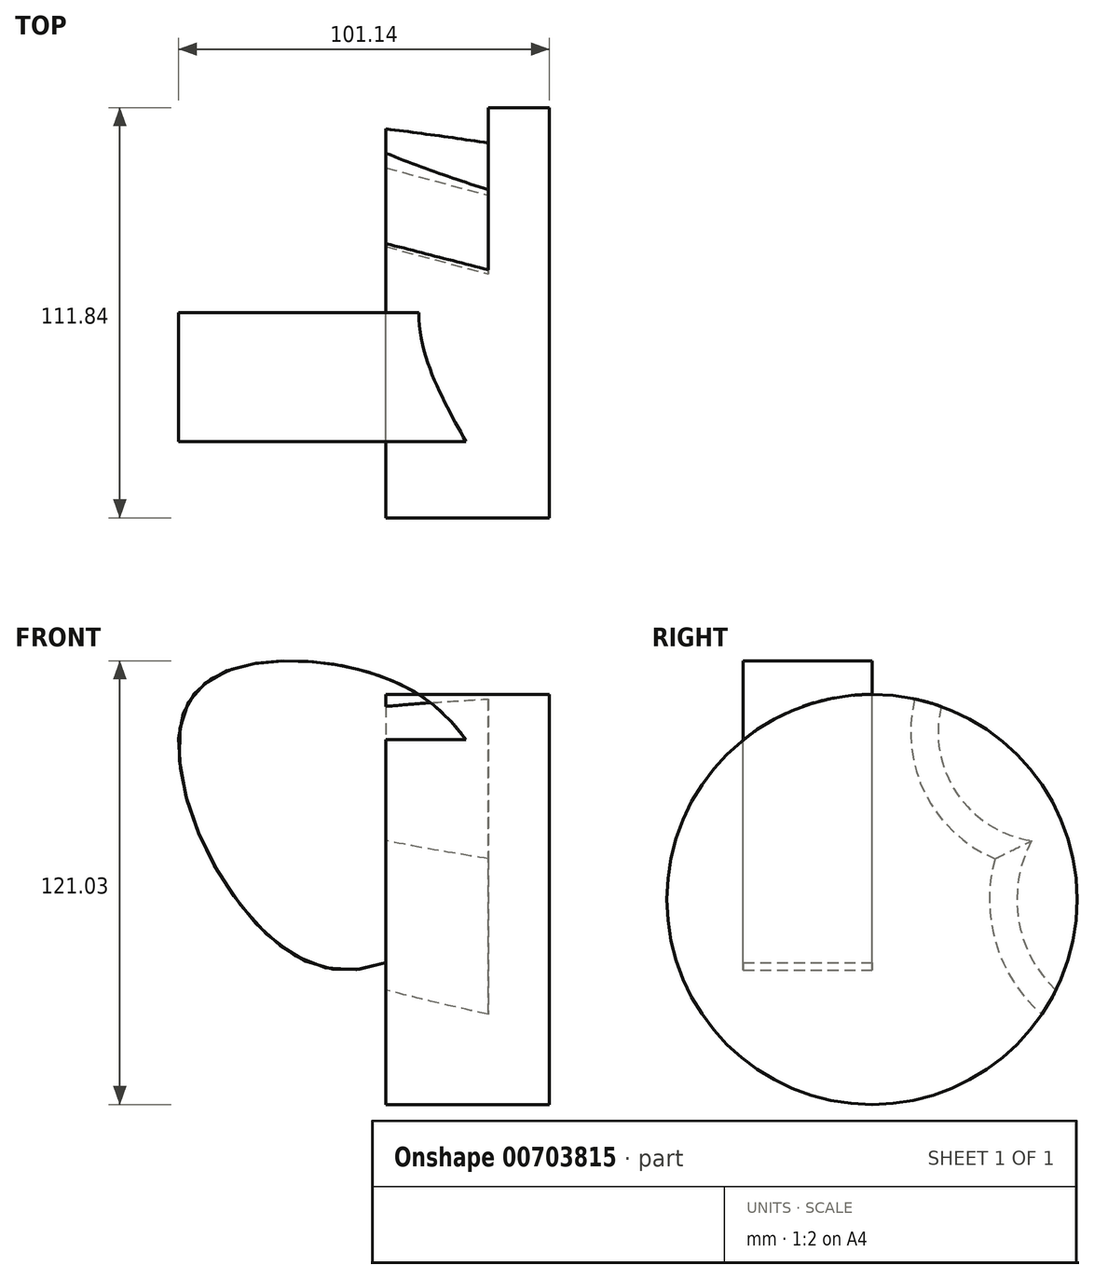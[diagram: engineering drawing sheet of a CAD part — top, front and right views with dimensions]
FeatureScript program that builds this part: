
annotation { "Feature Type Name" : "Feature", "Feature Type Description" : "" }
export const myFeature = defineFeature(function(context is Context, id is Id, definition is map)
    precondition{}
    {
        {
            var Q0;
            Q0=qCreatedBy(makeId("Front.planeOp"),FACE);
            var sketch = newSketch(context, id + "F0", { "sketchPlane" : qUnion([Q0])});
            skFitSpline(sketch, "E0", {"points": [v(-55.14, 51) * mm, v(-13.96, 64.09) * mm, v(19.96, 46) * mm, v(26.63, 8.98) * mm, v(-19.5, -17.79) * mm, v(-55.14, 51) * mm]});
            skFitSpline(sketch, "E1.0", {"points": [v(-66.92, 53.66) * mm, v(-66.43, 55.13) * mm, v(-65.86, 56.57) * mm, v(-65, 58.44) * mm, v(-63.78, 60.66) * mm, v(-62.07, 63.12) * mm, v(-60.15, 65.36) * mm, v(-58.06, 67.36) * mm, v(-55.12, 69.7) * mm, v(-51.2, 72.07) * mm, v(-46.33, 74.14) * mm, v(-41.36, 75.57) * mm, v(-36.36, 76.5) * mm, v(-31.36, 77) * mm, v(-26.4, 77.16) * mm, v(-21.5, 77.01) * mm, v(-17.52, 76.67) * mm, v(-14.42, 76.3) * mm, v(-12.13, 75.96) * mm, v(-9.89, 75.57) * mm, v(-6.94, 75) * mm, v(-3.34, 74.14) * mm, v(0.84, 72.9) * mm, v(6.23, 70.95) * mm, v(12.6, 67.94) * mm, v(18.41, 64.12) * mm, v(22.68, 60.6) * mm, v(25.67, 57.72) * mm, v(28, 55.15) * mm, v(29.74, 53) * mm, v(32.26, 49.64) * mm, v(35.66, 44.16) * mm, v(39.1, 35.96) * mm, v(41.1, 26.93) * mm, v(41.22, 18.86) * mm, v(40.22, 12.25) * mm, v(39.1, 8.11) * mm, v(38.06, 5.23) * mm, v(37.4, 3.6) * mm, v(36.33, 1.16) * mm, v(34.48, -2.39) * mm, v(31.56, -6.92) * mm, v(28.21, -11.22) * mm, v(24.47, -15.26) * mm, v(20.35, -19) * mm, v(15.87, -22.4) * mm, v(11.04, -25.39) * mm, v(5.87, -27.88) * mm, v(0.37, -29.8) * mm, v(-5.46, -31) * mm, v(-10.53, -31.33) * mm, v(-14.66, -31.1) * mm, v(-17.79, -30.66) * mm, v(-20.4, -30.07) * mm, v(-22.46, -29.46) * mm, v(-24, -28.93) * mm, v(-25.52, -28.34) * mm, v(-27.5, -27.48) * mm, v(-29.88, -26.27) * mm, v(-32.63, -24.63) * mm, v(-36.13, -22.22) * mm, v(-40.24, -18.84) * mm, v(-44.77, -14.29) * mm, v(-48.95, -9.33) * mm, v(-54.05, -2.27) * mm, v(-58.45, 5.33) * mm, v(-62.07, 13.22) * mm, v(-64.38, 19.22) * mm, v(-66.23, 25.27) * mm, v(-67.6, 31.31) * mm, v(-68.44, 37.32) * mm, v(-68.62, 42.3) * mm, v(-68.39, 46.27) * mm, v(-68, 49.24) * mm, v(-67.48, 51.7) * mm, v(-66.92, 53.66) * mm, v(-66.43, 55.13) * mm, v(-65.86, 56.57) * mm, v(-66.92, 53.66) * mm]});
            skSolve(sketch);
        }
        {
            var Q0;
            Q0 = qSketchRegion(id + "F0", true);
            extrude(context, id + "F1", {"entities" : qUnion([Q0]), "depth" : 35.1 * mm, "offsetDistance" : 25.4 * mm});
        }
        {
            var Q0;
            Q0=qCreatedBy(makeId("Right.planeOp"),FACE);
            var sketch = newSketch(context, id + "F2", { "sketchPlane" : qUnion([Q0])});
            skCircle(sketch, "E2", {"center": v(0, 0) * mm, "radius": 55.92 * mm});
            skSolve(sketch);
        }
        {
            var Q0;
            Q0=makeQuery(id+"F2.imprint","IMPRINT",FACE,{"disambiguationData":[TD([[makeQuery(id+"F2.imprint","IMPRINT",EDGE,{"derivedFrom":sQuery(id+"F2.wireOp",EDGE,"E2")}),1.0]])]});
            extrude(context, id + "F3", {"entities" : qUnion([Q0]), "operationType" : NewBodyOperationType.ADD, "depth" : 44.6 * mm, "offsetDistance" : 25.4 * mm});
        }
        {
            var Q0;
            Q0=qCreatedBy(makeId("Right.planeOp"),FACE);
            var sketch = newSketch(context, id + "F4", { "sketchPlane" : qUnion([Q0])});
            skCircle(sketch, "E3", {"center": v(47.93, 45.63) * mm, "radius": 29.9 * mm});
            skCircle(sketch, "E4", {"center": v(73.6, 0) * mm, "radius": 34.1 * mm});
            skSolve(sketch);
        }
        {
            var Q0;
            Q0 = qSketchRegion(id + "F4", true);
            extrude(context, id + "F5", {"entities" : qUnion([Q0]), "operationType" : NewBodyOperationType.REMOVE, "depth" : 27.93 * mm, "offsetDistance" : 25.4 * mm, "hasDraft" : true, "draftAngle" : 15 * degree});
        }
    });
